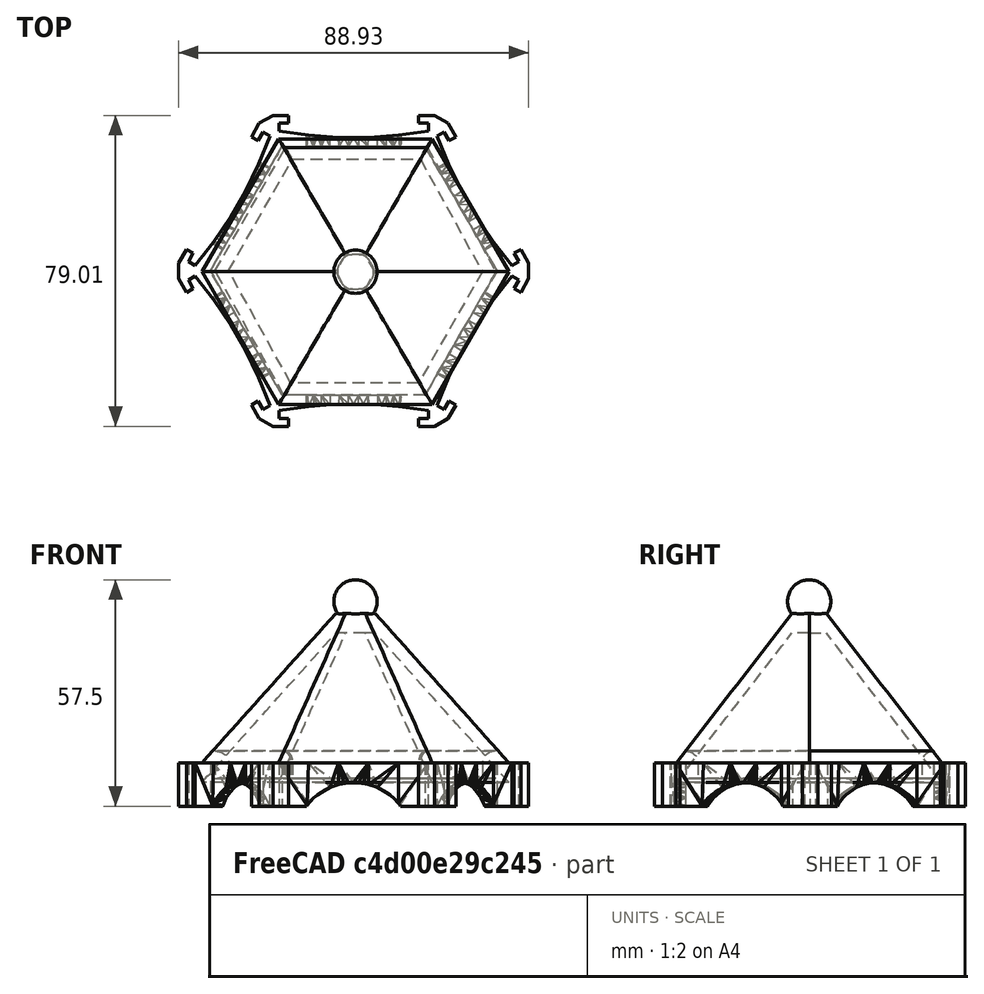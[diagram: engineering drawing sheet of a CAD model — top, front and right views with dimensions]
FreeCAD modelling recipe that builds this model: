
FCSTD DOCUMENT  (FreeCAD 0.16R)
Label: tapa exagono
License: All rights reserved
LicenseURL: http://en.wikipedia.org/wiki/All_rights_reserved
objects: Part::Feature×5, Part::RegularPolygon×2, Part::MultiFuse×2, Part::Loft×1, Part::Sphere×1, Part::Cylinder×1, Sketcher::SketchObject×1, PartDesign::Pad×1, Part::Thickness×1
note: 16 computed .brp shape members not serialized (recipe doc carries the construction recipe); baked Part::Feature solids carry a one-line shape summary decoded from their .brp

FEATURE [Part::RegularPolygon] RegularPolygon001  label="Polígono regular001"
  Circumradius = 39
  Placement = pos=(44,39,167) rot=(0,0,1;0rad)
  Polygon = 6
FEATURE [Part::RegularPolygon] RegularPolygon002  label="Polígono regular002"
  Circumradius = 5
  Placement = pos=(44,39,205) rot=(0,0,1;0rad)
  Polygon = 6
FEATURE [Part::Feature] Cut  label="Cut003"
  Placement = pos=(-0.942682,-0.269107,0) rot=(0,0,1;0rad)
  shape: bbox 88.93 x 79.01 x 11 mm, 641 faces (baked)
FEATURE [Part::Loft] Loft
  Closed = true
  Ruled = true
  Sections = -> [RegularPolygon001,RegularPolygon002]
  Solid = true
FEATURE [Part::Feature] Face
  shape: bbox 10 x 8.66 x 2e-07 mm, 1 faces, 0 solids (baked)
FEATURE [Part::Feature] Face001
  shape: bbox 78 x 67.55 x 2e-07 mm, 1 faces, 0 solids (baked)
FEATURE [Part::Feature] Shell
  Placement = pos=(0,0,5) rot=(0,0,1;0rad)
  shape: bbox 78 x 67.55 x 38 mm, 8 faces, 0 solids (baked)
FEATURE [Part::Sphere] Sphere  label="Esfera"
  Angle1 = -90
  Angle2 = 90
  Angle3 = 360
  Placement = pos=(44,39,213) rot=(0,0,1;0rad)
  Radius = 5.5
FEATURE [Part::Cylinder] Cylinder  label="Cilindro"
  Angle = 360
  Height = 10
  Placement = pos=(44,39,205) rot=(0,0,1;0rad)
  Radius = 3
FEATURE [Part::MultiFuse] Fusion
  Shapes = -> [Cylinder,Sphere]
FEATURE [Part::Feature] Solid
  shape: bbox 78 x 67.55 x 38 mm, 8 faces (baked)
FEATURE [Part::MultiFuse] Fusion001
  Shapes = -> [Solid,Fusion]
FEATURE [Sketcher::SketchObject] Sketch
  Placement = pos=(0,0,172) rot=(1,0,0;3.14159rad)
  Support = -> Fusion001 [Face1]
  sketch-geometry (6):
    g0: LineSegment StartX=61.7849 StartY=-7.72586 StartZ=0 EndX=25.7467 EndY=-7.72586 EndZ=0
    g1: LineSegment StartX=25.7467 StartY=-7.72586 StartZ=0 EndX=8.36928 EndY=-39.2977 EndZ=0
    g2: LineSegment StartX=8.36928 StartY=-39.2977 StartZ=0 EndX=26.2302 EndY=-70.5985 EndZ=0
    g3: LineSegment StartX=26.2302 StartY=-70.5985 StartZ=0 EndX=62.2684 EndY=-70.5985 EndZ=0
    g4: LineSegment StartX=62.2684 StartY=-70.5985 StartZ=0 EndX=79.6458 EndY=-39.0267 EndZ=0
    g5: LineSegment StartX=79.6458 StartY=-39.0267 StartZ=0 EndX=61.7849 EndY=-7.72586 EndZ=0
  constraints (9):
    c: Coincident(g0,g1)
    c: Coincident(g1,g2)
    c: Coincident(g2,g3)
    c: Coincident(g3,g4)
    c: Coincident(g4,g5)
    c: Coincident(g5,g0)
    c: Equal(g0, g1-g5) x5
    c: Horizontal(g0)
    c: Horizontal(g3)
FEATURE [PartDesign::Pad] Pad
  Length = 4
  Length2 = 100
  Sketch = -> Sketch
  Type = 0
FEATURE [Part::Thickness] Thickness
  Faces = -> Pad [Face1]
  Intersection = false
  Join = 0
  Mode = 0
  SelfIntersection = false
  Value = -3
